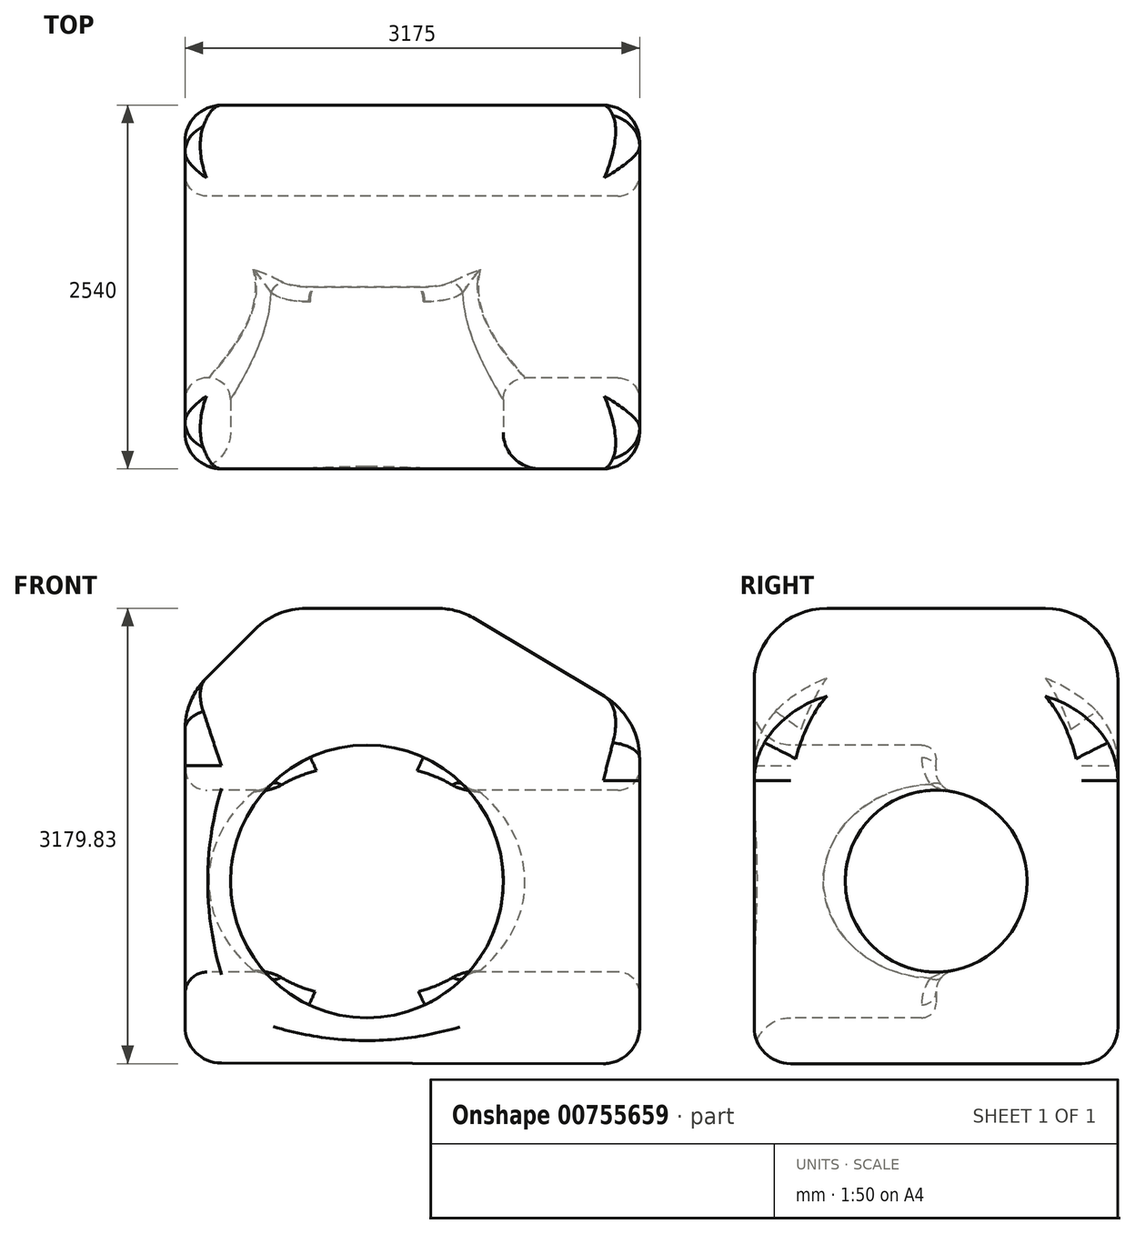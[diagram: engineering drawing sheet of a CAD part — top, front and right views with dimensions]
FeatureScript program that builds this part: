
annotation { "Feature Type Name" : "Feature", "Feature Type Description" : "" }
export const myFeature = defineFeature(function(context is Context, id is Id, definition is map)
    precondition{}
    {
        {
            var Q0;
            Q0=qCreatedBy(makeId("Front.planeOp"),FACE);
            var sketch = newSketch(context, id + "F0", { "sketchPlane" : qUnion([Q0])});
            skLineSegment(sketch, "E0", {"start": v(-1824.65, -1596.72) * mm, "end": v(-1824.65, 943.28) * mm});
            skLineSegment(sketch, "E1", {"start": v(-1824.65, 943.28) * mm, "end": v(-1189.65, 1578.28) * mm});
            skLineSegment(sketch, "E2", {"start": v(-1189.65, 1578.28) * mm, "end": v(80.35, 1578.28) * mm});
            skLineSegment(sketch, "E3", {"start": v(80.35, 1578.28) * mm, "end": v(1350.35, 816.28) * mm});
            skLineSegment(sketch, "E4", {"start": v(1350.35, 816.28) * mm, "end": v(1350.35, -1601.98) * mm});
            skLineSegment(sketch, "E5", {"start": v(1350.35, -1601.98) * mm, "end": v(-1824.65, -1596.72) * mm});
            skSolve(sketch);
        }
        {
            var Q0;
            Q0 = qSketchRegion(id + "F0", true);
            extrude(context, id + "F1", {"entities" : qUnion([Q0]), "depth" : 2540 * mm, "offsetDistance" : 25.4 * mm});
        }
        {
            var Q0;
            Q0=makeQuery(id+"F1.opExtrude","CAP_FACE",FACE,{"disambiguationData":[OSD([sQuery(id+"F0.wireOp",EDGE,"E0"),sQuery(id+"F0.wireOp",EDGE,"E1"),sQuery(id+"F0.wireOp",EDGE,"E2"),sQuery(id+"F0.wireOp",EDGE,"E3"),sQuery(id+"F0.wireOp",EDGE,"E4"),sQuery(id+"F0.wireOp",EDGE,"E5")])],"isStart":false});
            var sketch = newSketch(context, id + "F2", { "sketchPlane" : qUnion([Q0])});
            skCircle(sketch, "E6", {"center": v(-554.65, -328.82) * mm, "radius": 952.5 * mm});
            skSolve(sketch);
        }
        {
            var Q0;
            Q0 = qSketchRegion(id + "F2", true);
            extrude(context, id + "F3", {"entities" : qUnion([Q0]), "operationType" : NewBodyOperationType.REMOVE, "depth" : -1270 * mm, "offsetDistance" : 25.4 * mm});
        }
        {
            var Q0;
            Q0=makeQuery(id+"F1.opExtrude","SWEPT_FACE",FACE,{"disambiguationData":[OSD([sQuery(id+"F0.wireOp",EDGE,"E0")])]});
            var sketch = newSketch(context, id + "F4", { "sketchPlane" : qUnion([Q0])});
            skCircle(sketch, "E7", {"center": v(1270, -326.72) * mm, "radius": 635 * mm});
            skSolve(sketch);
        }
        {
            var Q0;
            Q0=makeQuery(id+"F4.imprint","IMPRINT",FACE,{"disambiguationData":[TD([[makeQuery(id+"F4.imprint","IMPRINT",EDGE,{"derivedFrom":sQuery(id+"F4.wireOp",EDGE,"E7")}),1.0]])]});
            extrude(context, id + "F5", {"entities" : qUnion([Q0]), "operationType" : NewBodyOperationType.REMOVE, "endBound" : BoundingType.THROUGH_ALL, "oppositeDirection" : true, "depth" : 25.4 * mm, "offsetDistance" : 25.4 * mm});
        }
        {
            var Q0;
            Q0=makeQuery(id+"F5.boolean.opBoolean","INTERSECT",EDGE,{"disambiguationData":[OD(0.0)],"derivedFrom":[makeQuery(id+"F3.boolean.opBoolean","COPY",FACE,{"derivedFrom":makeQuery(id+"F3.opExtrude","CAP_FACE",FACE,{"disambiguationData":[OSD([sQuery(id+"F2.wireOp",EDGE,"E6")])],"isStart":false})}),makeQuery(id+"F5.opExtrude","SWEPT_FACE",FACE,{"disambiguationData":[OSD([sQuery(id+"F4.wireOp",EDGE,"E7")])]})]});
            var Q1;
            Q1=makeQuery(id+"F5.boolean.opBoolean","COPY",FACE,{"derivedFrom":makeQuery(id+"F5.opExtrude","SWEPT_FACE",FACE,{"disambiguationData":[OSD([sQuery(id+"F4.wireOp",EDGE,"E7")])]})});
            fillet(context, id + "F6", {"entities" : qUnion([Q0, Q1]), "radius" : 152.4 * mm, "tangentPropagation" : true, "allowEdgeOverflow" : false});
        }
        {
            var Q0;
            Q0=makeQuery(id+"F1.opExtrude","SWEPT_FACE",FACE,{"disambiguationData":[OSD([sQuery(id+"F0.wireOp",EDGE,"E1")])]});
            var Q1;
            Q1=makeQuery(id+"F1.opExtrude","SWEPT_FACE",FACE,{"disambiguationData":[OSD([sQuery(id+"F0.wireOp",EDGE,"E2")])]});
            var Q2;
            Q2=makeQuery(id+"F1.opExtrude","SWEPT_FACE",FACE,{"disambiguationData":[OSD([sQuery(id+"F0.wireOp",EDGE,"E3")])]});
            fillet(context, id + "F7", {"entities" : qUnion([Q0, Q1, Q2]), "radius" : 508 * mm, "tangentPropagation" : true, "allowEdgeOverflow" : false});
        }
        {
            var Q0;
            Q0=makeQuery(id+"F1.opExtrude","CAP_FACE",FACE,{"disambiguationData":[OSD([sQuery(id+"F0.wireOp",EDGE,"E0"),sQuery(id+"F0.wireOp",EDGE,"E1"),sQuery(id+"F0.wireOp",EDGE,"E2"),sQuery(id+"F0.wireOp",EDGE,"E3"),sQuery(id+"F0.wireOp",EDGE,"E4"),sQuery(id+"F0.wireOp",EDGE,"E5")])],"isStart":false});
            var Q1;
            Q1=makeQuery(id+"F1.opExtrude","CAP_FACE",FACE,{"disambiguationData":[OSD([sQuery(id+"F0.wireOp",EDGE,"E0"),sQuery(id+"F0.wireOp",EDGE,"E1"),sQuery(id+"F0.wireOp",EDGE,"E2"),sQuery(id+"F0.wireOp",EDGE,"E3"),sQuery(id+"F0.wireOp",EDGE,"E4"),sQuery(id+"F0.wireOp",EDGE,"E5")])],"isStart":true});
            var Q2;
            Q2=makeQuery(id+"F1.opExtrude","SWEPT_FACE",FACE,{"disambiguationData":[OSD([sQuery(id+"F0.wireOp",EDGE,"E5")])]});
            fillet(context, id + "F8", {"entities" : qUnion([Q0, Q1, Q2]), "radius" : 254 * mm, "tangentPropagation" : true, "allowEdgeOverflow" : false});
        }
        {
            var Q0;
            Q0=makeQuery(id+"F3.boolean.opBoolean","COPY",FACE,{"derivedFrom":makeQuery(id+"F3.opExtrude","SWEPT_FACE",FACE,{"disambiguationData":[OSD([sQuery(id+"F2.wireOp",EDGE,"E6")])]})});
            fillet(context, id + "F9", {"entities" : qUnion([Q0]), "radius" : 101.6 * mm, "tangentPropagation" : true, "allowEdgeOverflow" : false});
        }
    });
